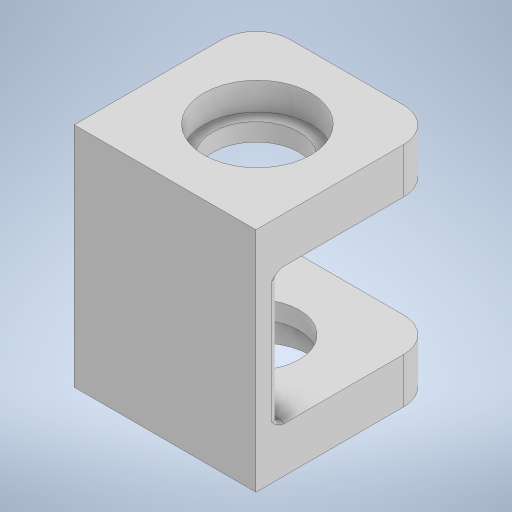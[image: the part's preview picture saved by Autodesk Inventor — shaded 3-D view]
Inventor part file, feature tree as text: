
AUTODESK INVENTOR PART (.ipt)
format: ipt  version: 2023.2 (Build 272271030, 271C)  size: 641,536 bytes
history: native  units: mm
features: extrude x6, sketch x6, projected_geometry x4, fillet x2
ambient origin geometry x8: Origin, YZ Plane, XZ Plane, XY Plane, X Axis, Y Axis, Z Axis, Center Point
bodies: Solid1 (feature_tree)
feature tree (18):
  extrude  "Extrusion1"  Depth=10.0mm
  extrude  "Extrusion2"  Depth=80.0mm
  extrude  "Extrusion6"  Depth=20.0mm
  fillet  "Fillet1"  Radius=70.0mm
  fillet  "Fillet2"  Radius=15.0mm
  extrude  "Extrusion15"  Depth=3.0mm
  extrude  "Extrusion17"  Depth=110.0mm TaperAngle=0.0deg
  extrude  "Extrusion18"  Depth=7.8mm TaperAngle=0.0deg
  sketch  "Sketch1"  dims[d0=20.0mm d1=0.0mm d2=10.0mm]
  sketch  "Sketch2"  dims[d3=80.0mm d4=0.0mm d11=80.0mm]
  projected_geometry  "Projected Loop1"
  projected_geometry  "Projected Loop4"
  sketch  "Sketch8"  dims[d12=80.0mm d16=20.0mm d17=70.0mm d18=0.0mm d19=15.0mm]
  sketch  "Sketch17"  dims[d39=3.0mm d56=17.0mm]
  projected_geometry  "Projected Loop8"
  sketch  "Sketch19"  dims[d57=47.2mm d58=110.0mm d59=0.0mm]
  projected_geometry  "Projected Loop9"
  sketch  "Sketch20"  dims[d63=38.0mm d64=7.8mm d65=0.0mm d66=38.0mm d67=7.8mm d68=0.0mm]
